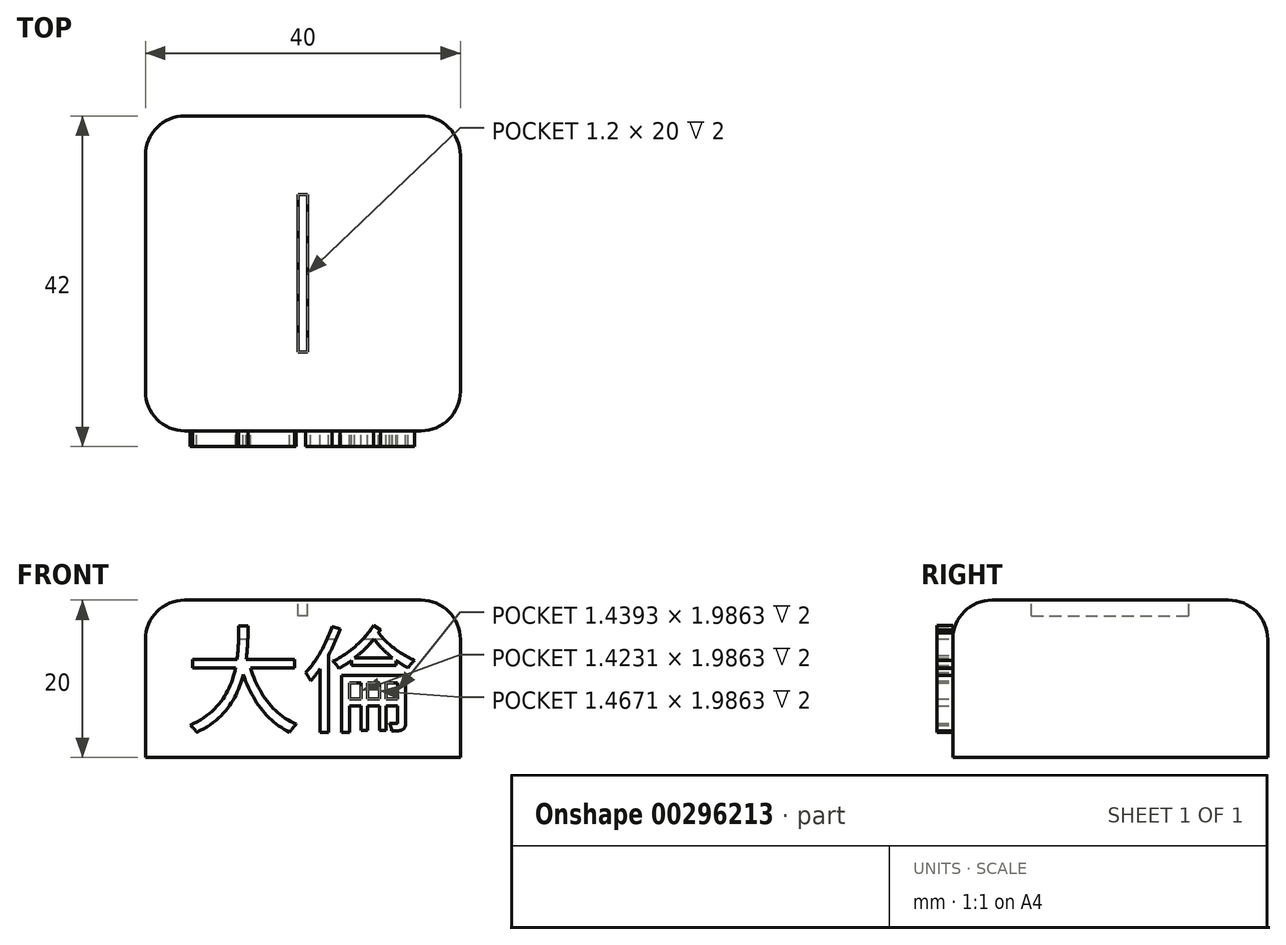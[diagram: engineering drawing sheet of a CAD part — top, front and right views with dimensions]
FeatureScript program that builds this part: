
annotation { "Feature Type Name" : "Feature", "Feature Type Description" : "" }
export const myFeature = defineFeature(function(context is Context, id is Id, definition is map)
    precondition{}
    {
        {
            var Q0;
            Q0=qCreatedBy(makeId("Top.planeOp"),FACE);
            var sketch = newSketch(context, id + "F0", { "sketchPlane" : qUnion([Q0])});
            skLineSegment(sketch, "E0.bottom", {"start": v(20, -20) * mm, "end": v(-20, -20) * mm});
            skLineSegment(sketch, "E0.top", {"start": v(20, 20) * mm, "end": v(-20, 20) * mm});
            skLineSegment(sketch, "E0.left", {"start": v(20, -20) * mm, "end": v(20, 20) * mm});
            skLineSegment(sketch, "E0.right", {"start": v(-20, -20) * mm, "end": v(-20, 20) * mm});
            skPoint(sketch, "E0.middle", {"position": v(0, 0) * mm});
            skLineSegment(sketch, "E1.bottom", {"start": v(0.6, -10) * mm, "end": v(-0.6, -10) * mm});
            skLineSegment(sketch, "E1.top", {"start": v(0.6, 10) * mm, "end": v(-0.6, 10) * mm});
            skLineSegment(sketch, "E1.left", {"start": v(0.6, -10) * mm, "end": v(0.6, 10) * mm});
            skLineSegment(sketch, "E1.right", {"start": v(-0.6, -10) * mm, "end": v(-0.6, 10) * mm});
            skSolve(sketch);
        }
        {
            var Q0;
            Q0=makeQuery(id+"F0.imprint","IMPRINT",FACE,{"disambiguationData":[TD([[makeQuery(id+"F0.imprint","IMPRINT",EDGE,{"derivedFrom":sQuery(id+"F0.wireOp",EDGE,"E0.bottom")}),-1.0]])]});
            var Q1;
            Q1=makeQuery(id+"F0.imprint","IMPRINT",FACE,{"disambiguationData":[TD([[makeQuery(id+"F0.imprint","IMPRINT",EDGE,{"derivedFrom":sQuery(id+"F0.wireOp",EDGE,"E1.bottom")}),-1.0]])]});
            extrude(context, id + "F1", {"entities" : qUnion([Q0, Q1]), "oppositeDirection" : true, "depth" : 20 * mm});
        }
        {
            var Q0;
            Q0=makeQuery(id+"F0.imprint","IMPRINT",FACE,{"disambiguationData":[TD([[makeQuery(id+"F0.imprint","IMPRINT",EDGE,{"derivedFrom":sQuery(id+"F0.wireOp",EDGE,"E1.bottom")}),-1.0]])]});
            extrude(context, id + "F2", {"entities" : qUnion([Q0]), "operationType" : NewBodyOperationType.REMOVE, "oppositeDirection" : true, "depth" : 2 * mm});
        }
        {
            var Q0;
            Q0=makeQuery(id+"F2.boolean.opBoolean","COPY",EDGE,{"derivedFrom":makeQuery(id+"F2.opExtrude","CAP_EDGE",EDGE,{"disambiguationData":[OSD([sQuery(id+"F0.wireOp",EDGE,"E1.left")])],"isStart":true})});
            var Q1;
            Q1=makeQuery(id+"F2.boolean.opBoolean","COPY",EDGE,{"derivedFrom":makeQuery(id+"F2.opExtrude","CAP_EDGE",EDGE,{"disambiguationData":[OSD([sQuery(id+"F0.wireOp",EDGE,"E1.right")])],"isStart":true})});
            var Q2;
            Q2=makeQuery(id+"F1.opExtrude","SWEPT_EDGE",EDGE,{"disambiguationData":[OSD([sQuery(id+"F0.wireOp",EDGE,"E0.bottom"),sQuery(id+"F0.wireOp",EDGE,"E0.left")])]});
            var Q3;
            Q3=makeQuery(id+"F1.opExtrude","SWEPT_EDGE",EDGE,{"disambiguationData":[OSD([sQuery(id+"F0.wireOp",EDGE,"E0.top"),sQuery(id+"F0.wireOp",EDGE,"E0.left")])]});
            var Q4;
            Q4=makeQuery(id+"F1.opExtrude","CAP_EDGE",EDGE,{"disambiguationData":[OSD([sQuery(id+"F0.wireOp",EDGE,"E0.left")])],"isStart":true});
            var Q5;
            Q5=makeQuery(id+"F1.opExtrude","SWEPT_EDGE",EDGE,{"disambiguationData":[OSD([sQuery(id+"F0.wireOp",EDGE,"E0.bottom"),sQuery(id+"F0.wireOp",EDGE,"E0.right")])]});
            var Q6;
            Q6=makeQuery(id+"F1.opExtrude","SWEPT_EDGE",EDGE,{"disambiguationData":[OSD([sQuery(id+"F0.wireOp",EDGE,"E0.top"),sQuery(id+"F0.wireOp",EDGE,"E0.right")])]});
            var Q7;
            Q7=makeQuery(id+"F1.opExtrude","CAP_EDGE",EDGE,{"disambiguationData":[OSD([sQuery(id+"F0.wireOp",EDGE,"E0.top")])],"isStart":true});
            var Q8;
            Q8=makeQuery(id+"F1.opExtrude","CAP_EDGE",EDGE,{"disambiguationData":[OSD([sQuery(id+"F0.wireOp",EDGE,"E0.right")])],"isStart":true});
            var Q9;
            Q9=makeQuery(id+"F1.opExtrude","CAP_EDGE",EDGE,{"disambiguationData":[OSD([sQuery(id+"F0.wireOp",EDGE,"E0.bottom")])],"isStart":true});
            fillet(context, id + "F3", {"entities" : qUnion([Q0, Q1, Q2, Q3, Q4, Q5, Q6, Q7, Q8, Q9]), "radius" : 5 * mm, "tangentPropagation" : true, "allowEdgeOverflow" : false});
        }
        {
            var Q0;
            Q0=makeQuery(id+"F1.opExtrude","SWEPT_FACE",FACE,{"disambiguationData":[OSD([sQuery(id+"F0.wireOp",EDGE,"E0.bottom")])]});
            var sketch = newSketch(context, id + "F4", { "sketchPlane" : qUnion([Q0])});
            skText(sketch, "E2", { "text": "大倫", "fontName": "NotoSansCJKtc-Regular.otf"});
            const initialGuessF4  = {"E2": [-0.015, -0.01568, 1, 0, 0.01068]};
            skSetInitialGuess(sketch, initialGuessF4);
            skSolve(sketch);
        }
        {
            var Q0;
            Q0=qSketchRegion(id+"F4",true);
            extrude(context, id + "F5", {"entities" : qUnion([Q0]), "operationType" : NewBodyOperationType.ADD, "depth" : 2 * mm});
        }
    });
